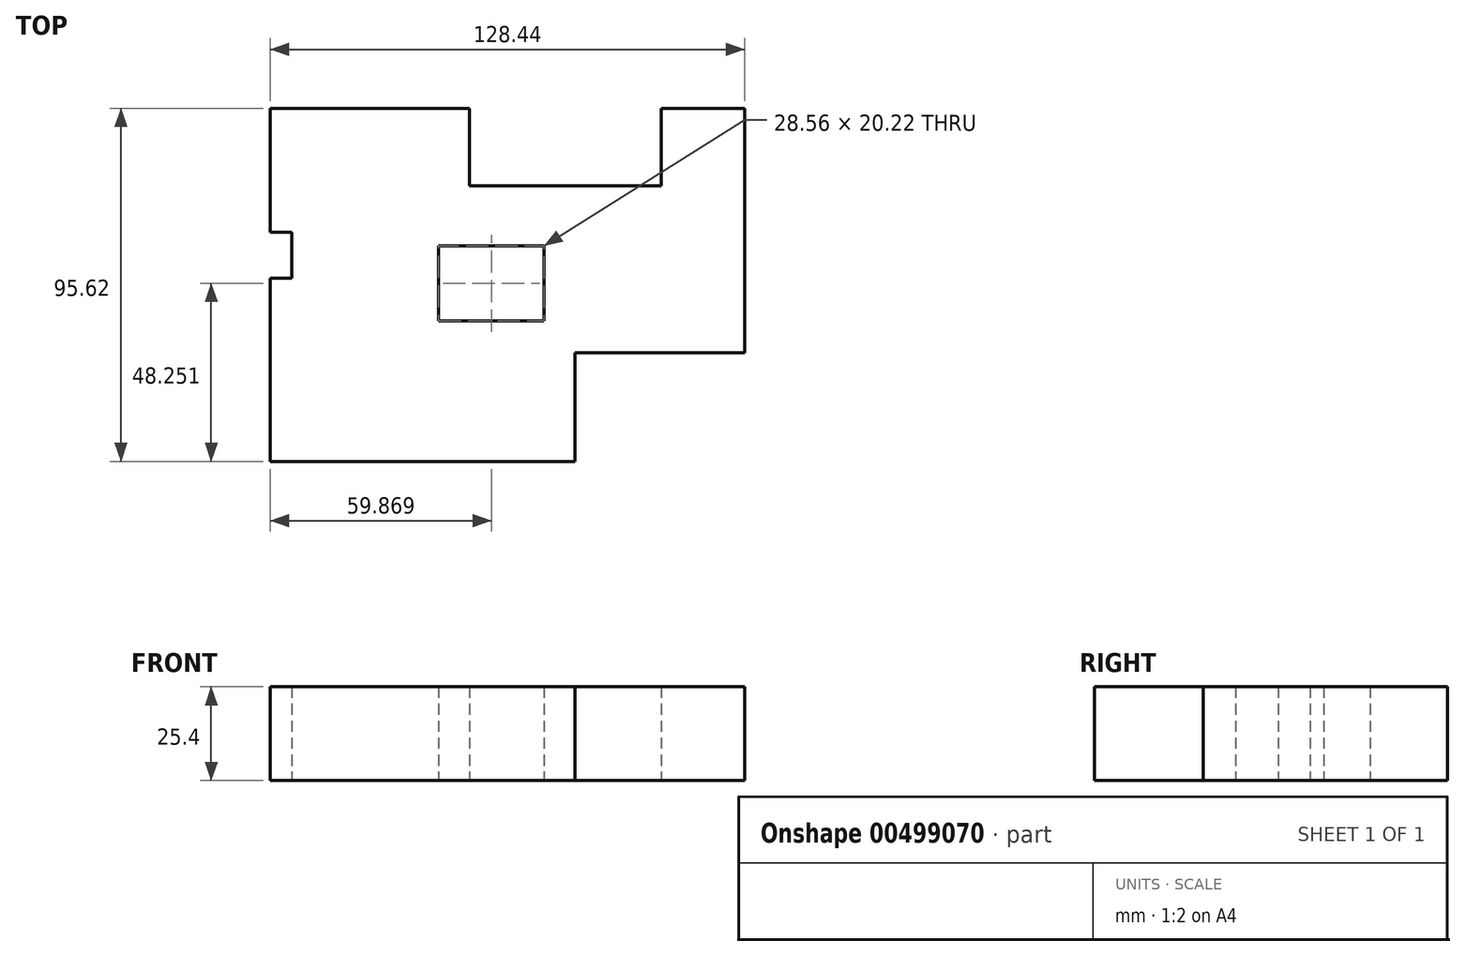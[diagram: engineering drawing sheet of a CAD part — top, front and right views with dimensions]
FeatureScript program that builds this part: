
annotation { "Feature Type Name" : "Feature", "Feature Type Description" : "" }
export const myFeature = defineFeature(function(context is Context, id is Id, definition is map)
    precondition{}
    {
        {
            var Q0;
            Q0=qCreatedBy(makeId("Top.planeOp"),FACE);
            var sketch = newSketch(context, id + "F0", { "sketchPlane" : qUnion([Q0])});
            skLineSegment(sketch, "E0.bottom", {"start": v(-61.2, 45.95) * mm, "end": v(67.24, 45.95) * mm});
            skLineSegment(sketch, "E0.top", {"start": v(-61.2, -49.67) * mm, "end": v(67.24, -49.67) * mm});
            skLineSegment(sketch, "E0.left", {"start": v(-61.2, 45.95) * mm, "end": v(-61.2, -49.67) * mm});
            skLineSegment(sketch, "E0.right", {"start": v(67.24, 45.95) * mm, "end": v(67.24, -49.67) * mm});
            skLineSegment(sketch, "E1.bottom", {"start": v(-77.88, 0) * mm, "end": v(-55.35, 0) * mm});
            skLineSegment(sketch, "E1.top", {"start": v(-77.88, 12.42) * mm, "end": v(-55.35, 12.42) * mm});
            skLineSegment(sketch, "E1.left", {"start": v(-77.88, 0) * mm, "end": v(-77.88, 12.42) * mm});
            skLineSegment(sketch, "E1.right", {"start": v(-55.35, 0) * mm, "end": v(-55.35, 12.42) * mm});
            skLineSegment(sketch, "E2.bottom", {"start": v(-7.27, 47.9) * mm, "end": v(44.7, 47.9) * mm});
            skLineSegment(sketch, "E2.top", {"start": v(-7.27, 25.01) * mm, "end": v(44.7, 25.01) * mm});
            skLineSegment(sketch, "E2.left", {"start": v(-7.27, 47.9) * mm, "end": v(-7.27, 25.01) * mm});
            skLineSegment(sketch, "E2.right", {"start": v(44.7, 47.9) * mm, "end": v(44.7, 25.01) * mm});
            skLineSegment(sketch, "E3.bottom", {"start": v(21.29, -20.22) * mm, "end": v(71.32, -20.22) * mm});
            skLineSegment(sketch, "E3.top", {"start": v(21.29, -53.75) * mm, "end": v(71.32, -53.75) * mm});
            skLineSegment(sketch, "E3.left", {"start": v(21.29, -20.22) * mm, "end": v(21.29, -53.75) * mm});
            skLineSegment(sketch, "E3.right", {"start": v(71.32, -20.22) * mm, "end": v(71.32, -53.75) * mm});
            skLineSegment(sketch, "E4.bottom", {"start": v(-15.61, 8.7) * mm, "end": v(12.95, 8.7) * mm});
            skLineSegment(sketch, "E4.top", {"start": v(-15.61, -11.53) * mm, "end": v(12.95, -11.53) * mm});
            skLineSegment(sketch, "E4.left", {"start": v(-15.61, 8.7) * mm, "end": v(-15.61, -11.53) * mm});
            skLineSegment(sketch, "E4.right", {"start": v(12.95, 8.7) * mm, "end": v(12.95, -11.53) * mm});
            skSolve(sketch);
        }
        {
            var Q0;
            {var subQ1=sQuery(id+"F0.wireOp",EDGE,"E1.right");Q0=makeQuery(id+"F0.imprint","IMPRINT",FACE,{"disambiguationData":[TD([[makeQuery(id+"F0.imprint","IMPRINT",EDGE,{"derivedFrom":subQ1}),-1.0]])]});}
            extrude(context, id + "F1", {"entities" : qUnion([Q0]), "depth" : 25.4 * mm});
        }
    });
